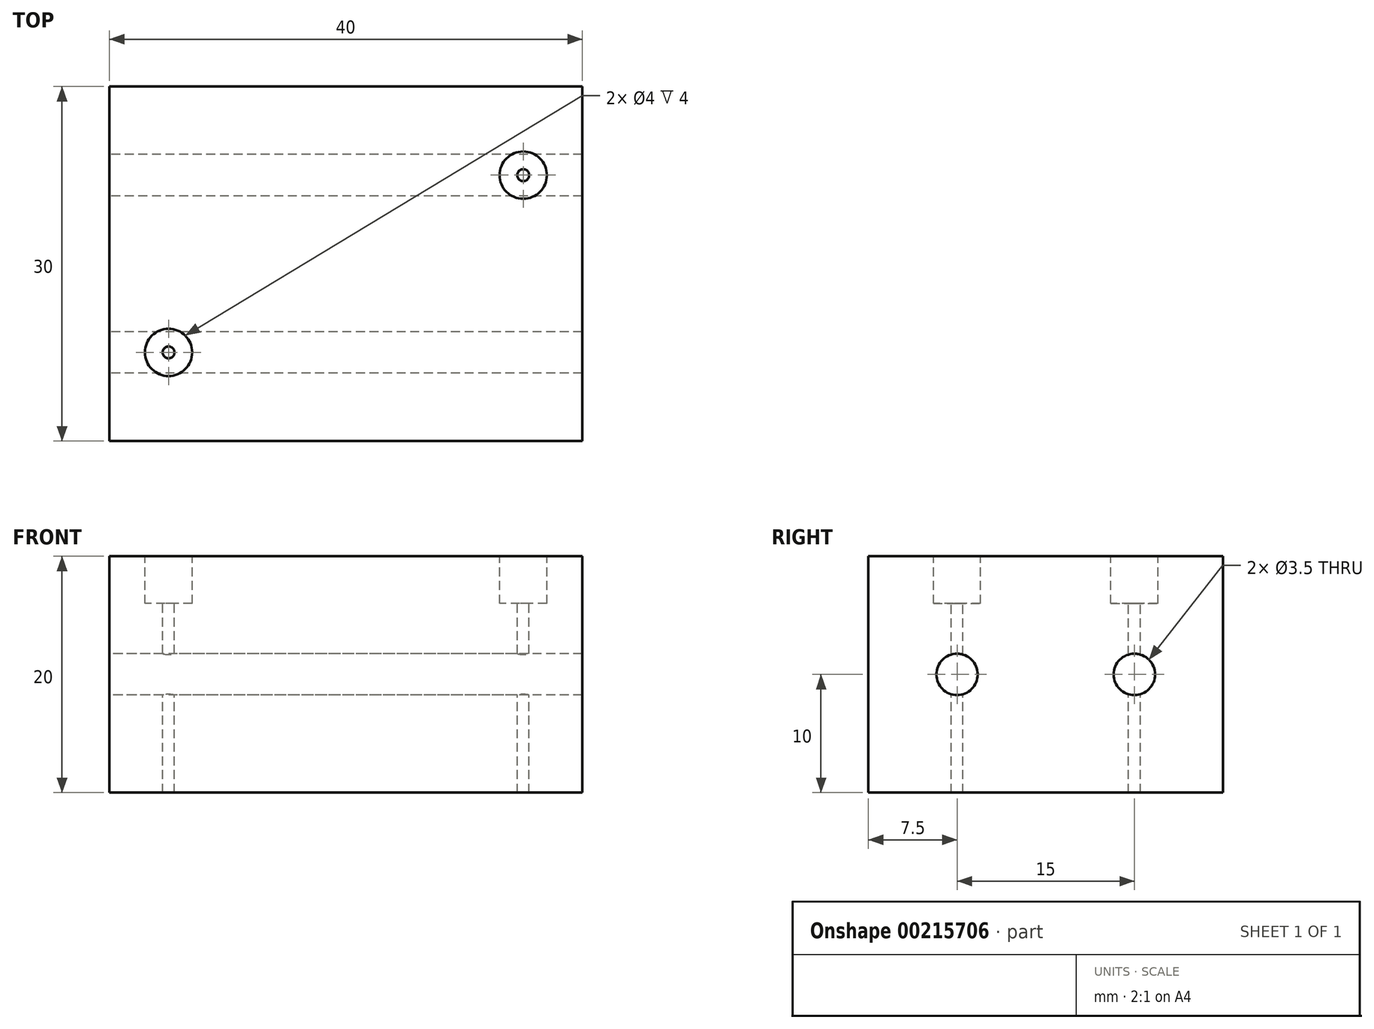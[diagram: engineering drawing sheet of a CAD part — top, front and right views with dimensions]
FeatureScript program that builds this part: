
annotation { "Feature Type Name" : "Feature", "Feature Type Description" : "" }
export const myFeature = defineFeature(function(context is Context, id is Id, definition is map)
    precondition{}
    {
        {
            var Q0;
            Q0=qCreatedBy(makeId("Top.planeOp"),FACE);
            var sketch = newSketch(context, id + "F0", { "sketchPlane" : qUnion([Q0])});
            skLineSegment(sketch, "E0.bottom", {"start": v(-20, -15) * mm, "end": v(20, -15) * mm});
            skLineSegment(sketch, "E0.top", {"start": v(-20, 15) * mm, "end": v(20, 15) * mm});
            skLineSegment(sketch, "E0.left", {"start": v(-20, -15) * mm, "end": v(-20, 15) * mm});
            skLineSegment(sketch, "E0.right", {"start": v(20, -15) * mm, "end": v(20, 15) * mm});
            skPoint(sketch, "E0.middle", {"position": v(0, 0) * mm});
            skSolve(sketch);
        }
        {
            var Q0;
            Q0 = qSketchRegion(id + "F0", true);
            extrude(context, id + "F1", {"entities" : qUnion([Q0]), "depth" : 20 * mm});
        }
        {
            var Q0;
            Q0=makeQuery(id+"F1.opExtrude","SWEPT_FACE",FACE,{"disambiguationData":[OSD([sQuery(id+"F0.wireOp",EDGE,"E0.left")])]});
            var sketch = newSketch(context, id + "F2", { "sketchPlane" : qUnion([Q0])});
            skCircle(sketch, "E1", {"center": v(-7.5, 10) * mm, "radius": 1.75 * mm});
            skCircle(sketch, "E2.MirrorC", {"center": v(7.5, 10) * mm, "radius": 1.75 * mm});
            skSolve(sketch);
        }
        {
            var Q0;
            Q0 = qSketchRegion(id + "F2", true);
            extrude(context, id + "F3", {"entities" : qUnion([Q0]), "operationType" : NewBodyOperationType.REMOVE, "endBound" : BoundingType.THROUGH_ALL, "oppositeDirection" : true, "depth" : 25 * mm});
        }
        {
            var Q0;
            Q0=makeQuery(id+"F1.opExtrude","CAP_FACE",FACE,{"disambiguationData":[OSD([sQuery(id+"F0.wireOp",EDGE,"E0.bottom"),sQuery(id+"F0.wireOp",EDGE,"E0.top"),sQuery(id+"F0.wireOp",EDGE,"E0.left"),sQuery(id+"F0.wireOp",EDGE,"E0.right")])],"isStart":false});
            var sketch = newSketch(context, id + "F4", { "sketchPlane" : qUnion([Q0])});
            skCircle(sketch, "E3", {"center": v(15, 7.5) * mm, "radius": 2 * mm});
            skCircle(sketch, "E4.2.0", {"center": v(-15, -7.5) * mm, "radius": 2 * mm});
            skPoint(sketch, "E4.center", {"position": v(0, 0) * mm});
            skLineSegment(sketch, "E4.anchor1", {"start": v(0, 0) * mm, "end": v(15, 7.5) * mm, "construction": true});
            skLineSegment(sketch, "E4.anchor2", {"start": v(0, 0) * mm, "end": v(-15, -7.5) * mm, "construction": true});
            skSolve(sketch);
        }
        {
            var Q0;
            Q0 = qSketchRegion(id + "F4", true);
            extrude(context, id + "F5", {"entities" : qUnion([Q0]), "operationType" : NewBodyOperationType.REMOVE, "oppositeDirection" : true, "depth" : 4 * mm});
        }
        {
            var Q0;
            Q0=makeQuery(id+"F5.boolean.opBoolean","COPY",FACE,{"derivedFrom":makeQuery(id+"F5.opExtrude","CAP_FACE",FACE,{"disambiguationData":[OSD([sQuery(id+"F4.wireOp",EDGE,"E3")])],"isStart":false})});
            var sketch = newSketch(context, id + "F6", { "sketchPlane" : qUnion([Q0])});
            skCircle(sketch, "E5", {"center": v(15, 7.5) * mm, "radius": 0.5 * mm});
            skCircle(sketch, "E6.2.0", {"center": v(-15, -7.5) * mm, "radius": 0.5 * mm});
            skPoint(sketch, "E6.center", {"position": v(0, 0) * mm});
            skLineSegment(sketch, "E6.anchor1", {"start": v(0, 0) * mm, "end": v(15, 7.5) * mm, "construction": true});
            skLineSegment(sketch, "E6.anchor2", {"start": v(0, 0) * mm, "end": v(-15, -7.5) * mm, "construction": true});
            skSolve(sketch);
        }
        {
            var Q0;
            Q0 = qSketchRegion(id + "F6", true);
            extrude(context, id + "F7", {"entities" : qUnion([Q0]), "operationType" : NewBodyOperationType.REMOVE, "endBound" : BoundingType.THROUGH_ALL, "oppositeDirection" : true, "depth" : 25 * mm});
        }
    });
